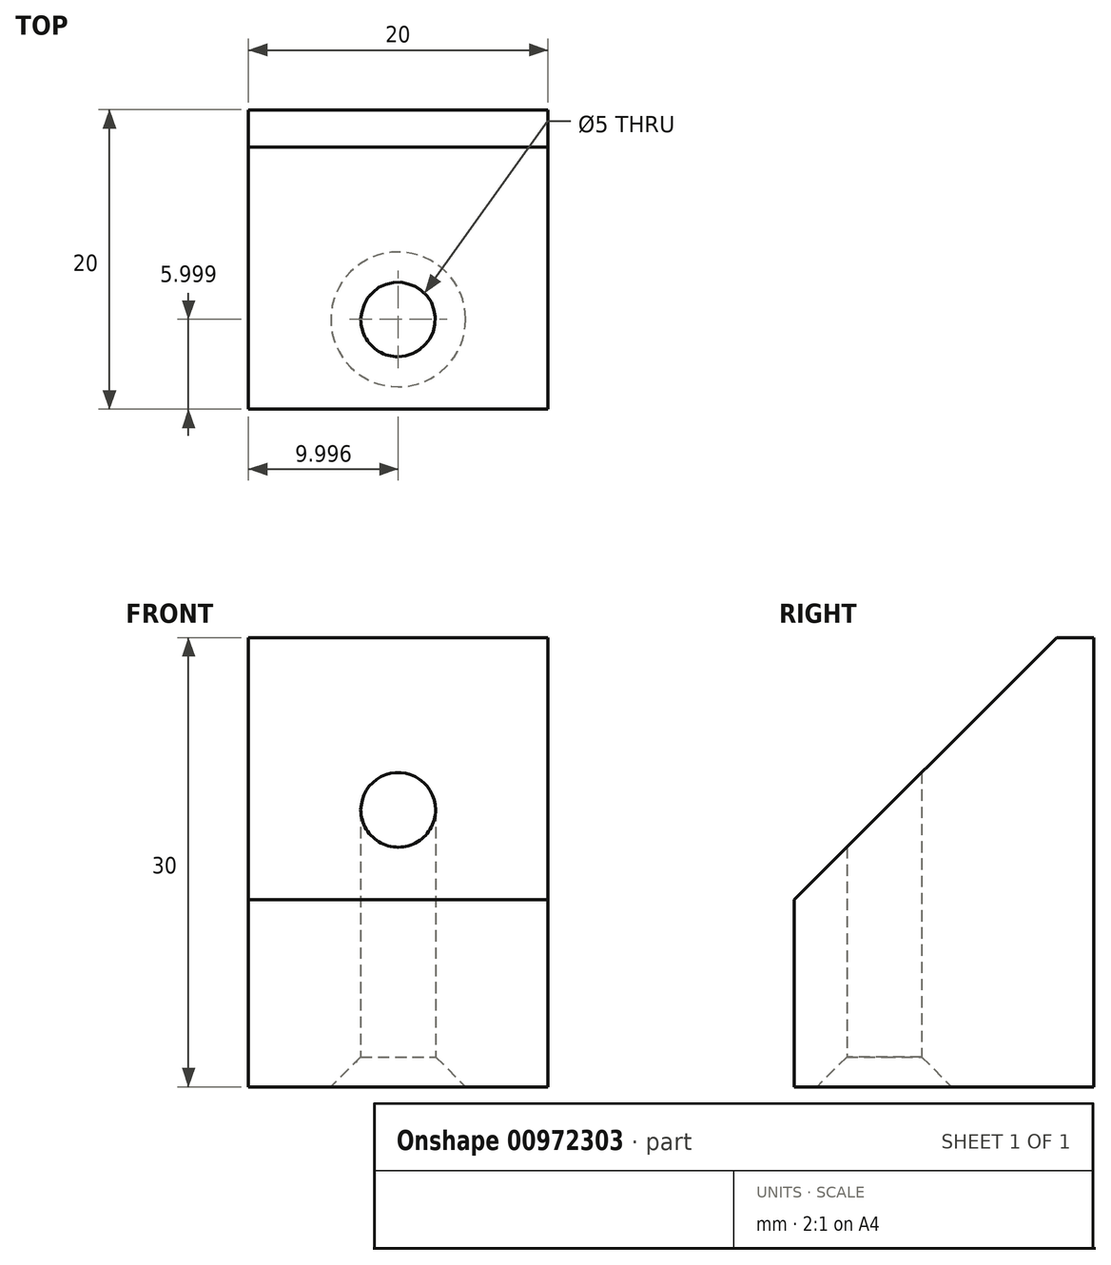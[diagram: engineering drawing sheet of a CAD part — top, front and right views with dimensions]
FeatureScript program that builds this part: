
annotation { "Feature Type Name" : "Feature", "Feature Type Description" : "" }
export const myFeature = defineFeature(function(context is Context, id is Id, definition is map)
    precondition{}
    {
        {
            var Q0;
            Q0=qCreatedBy(makeId("Top.planeOp"),FACE);
            var sketch = newSketch(context, id + "F0", { "sketchPlane" : qUnion([Q0])});
            skLineSegment(sketch, "E0.bottom", {"start": v(-14.1, 7.52) * mm, "end": v(5.9, 7.52) * mm});
            skLineSegment(sketch, "E0.top", {"start": v(-14.1, -12.48) * mm, "end": v(5.9, -12.48) * mm});
            skLineSegment(sketch, "E0.left", {"start": v(-14.1, 7.52) * mm, "end": v(-14.1, -12.48) * mm});
            skLineSegment(sketch, "E0.right", {"start": v(5.9, 7.52) * mm, "end": v(5.9, -12.48) * mm});
            skSolve(sketch);
        }
        {
            var Q0;
            Q0=makeQuery(id+"F0.imprint","IMPRINT",FACE,{"disambiguationData":[TD([[makeQuery(id+"F0.imprint","IMPRINT",EDGE,{"derivedFrom":sQuery(id+"F0.wireOp",EDGE,"E0.bottom")}),-1.0]])]});
            extrude(context, id + "F1", {"entities" : qUnion([Q0]), "depth" : 30 * mm, "offsetDistance" : 25 * mm});
        }
        {
            var Q0;
            Q0=makeQuery(id+"F1.opExtrude","CAP_EDGE",EDGE,{"disambiguationData":[OSD([sQuery(id+"F0.wireOp",EDGE,"E0.top")])],"isStart":false});
            chamfer(context, id + "F2", {"entities" : qUnion([Q0]), "width" : 17.5 * mm, "tangentPropagation" : true});
        }
        {
            var Q0;
            Q0=makeQuery(id+"F1.opExtrude","CAP_FACE",FACE,{"disambiguationData":[OSD([sQuery(id+"F0.wireOp",EDGE,"E0.bottom"),sQuery(id+"F0.wireOp",EDGE,"E0.top"),sQuery(id+"F0.wireOp",EDGE,"E0.left"),sQuery(id+"F0.wireOp",EDGE,"E0.right")])],"isStart":true});
            var sketch = newSketch(context, id + "F3", { "sketchPlane" : qUnion([Q0])});
            skCircle(sketch, "E1", {"center": v(-4.1, 6.48) * mm, "radius": 1.73 * mm});
            skPoint(sketch, "E1.centerSnap0", {"position": v(-4.1, 12.48) * mm});
            skLineSegment(sketch, "E2", {"start": v(-4.1, 6.48) * mm, "end": v(-4.1, 12.48) * mm, "construction": true});
            skSolve(sketch);
        }
        {
            var Q0;
            Q0=sQuery(id+"F3.wireOp",VERTEX,"E1.center");
            var Q1;
            Q1=makeQuery(id+"F1.opExtrude","SWEPT_BODY",BODY,{"disambiguationData":[OSD([sQuery(id+"F0.wireOp",EDGE,"E0.bottom"),sQuery(id+"F0.wireOp",EDGE,"E0.top"),sQuery(id+"F0.wireOp",EDGE,"E0.left"),sQuery(id+"F0.wireOp",EDGE,"E0.right")])]});
            hole(context, id + "F4", {"style" : HoleStyle.C_SINK, "endStyle" : HoleEndStyle.THROUGH, "holeDiameter" : 5 * mm, "cSinkDiameter" : 9 * mm, "cSinkAngle" : 90 * degree, "majorDiameter" : 5 * mm, "isTappedThrough" : true, "tappedDepth" : 12 * mm, "tapClearance" : 3, "locations" : qUnion([Q0]), "scope" : qUnion([Q1])});
        }
    });
